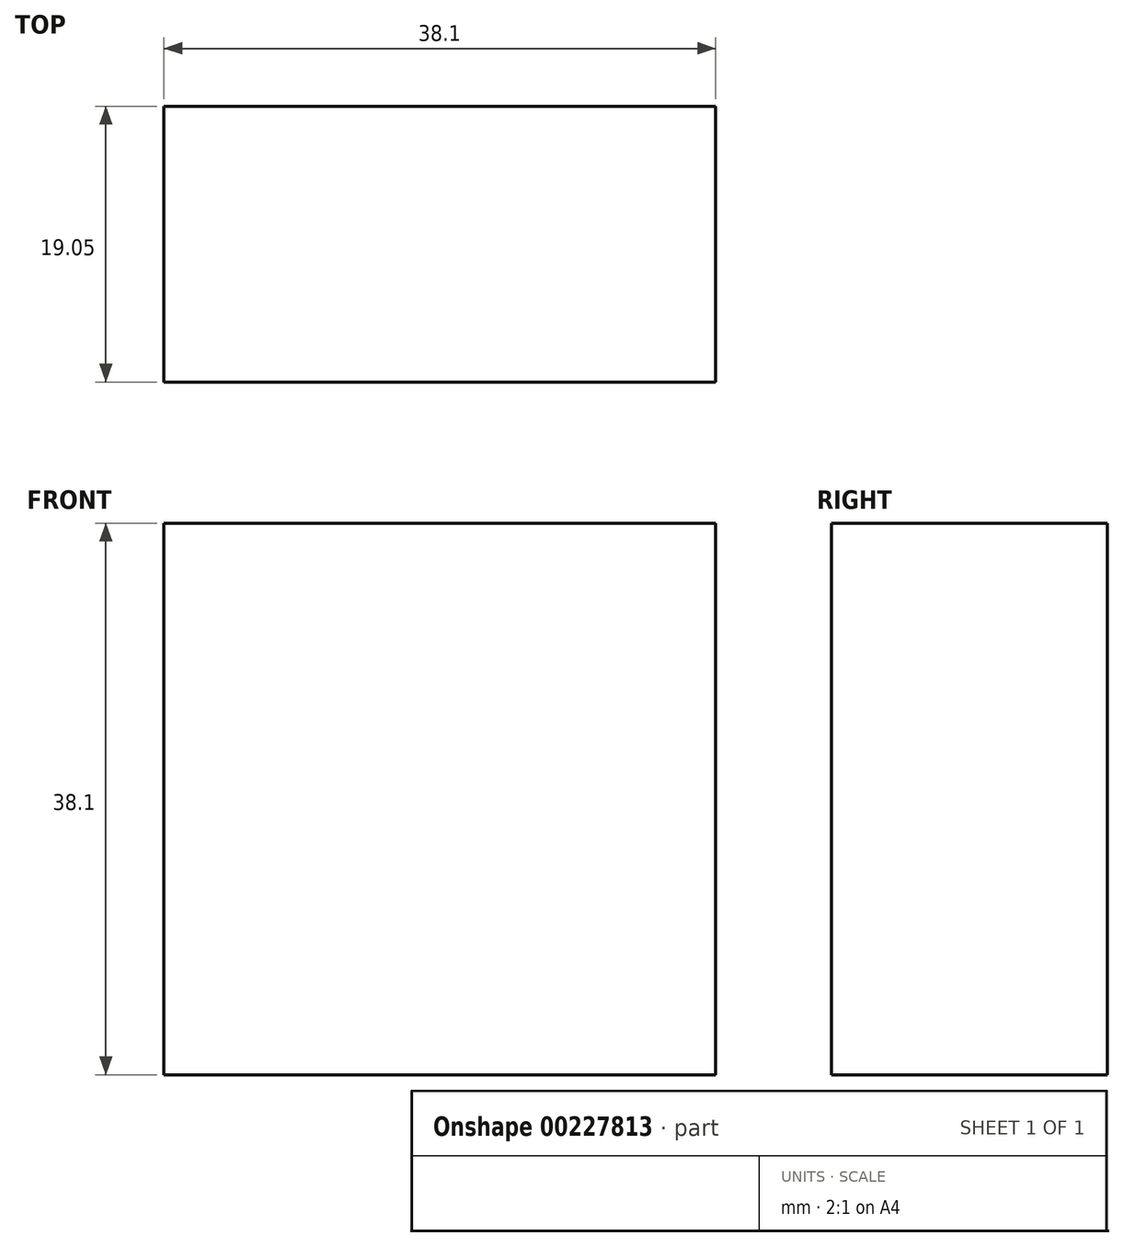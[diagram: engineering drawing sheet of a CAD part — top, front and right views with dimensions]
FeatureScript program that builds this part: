
annotation { "Feature Type Name" : "Feature", "Feature Type Description" : "" }
export const myFeature = defineFeature(function(context is Context, id is Id, definition is map)
    precondition{}
    {
        {
            var Q0;
            Q0=qCreatedBy(makeId("Front.planeOp"),FACE);
            var sketch = newSketch(context, id + "F0", { "sketchPlane" : qUnion([Q0])});
            skLineSegment(sketch, "E0.bottom", {"start": v(-30.4, 27.13) * mm, "end": v(7.7, 27.13) * mm});
            skLineSegment(sketch, "E0.top", {"start": v(-30.4, -10.97) * mm, "end": v(7.7, -10.97) * mm});
            skLineSegment(sketch, "E0.left", {"start": v(-30.4, 27.13) * mm, "end": v(-30.4, -10.97) * mm});
            skLineSegment(sketch, "E0.right", {"start": v(7.7, 27.13) * mm, "end": v(7.7, -10.97) * mm});
            skSolve(sketch);
        }
        {
            var Q0;
            Q0=makeQuery(id+"F0.imprint","IMPRINT",FACE,{"disambiguationData":[TD([[makeQuery(id+"F0.imprint","IMPRINT",EDGE,{"derivedFrom":sQuery(id+"F0.wireOp",EDGE,"E0.bottom")}),-1.0]])]});
            extrude(context, id + "F1", {"entities" : qUnion([Q0]), "depth" : 19.05 * mm});
        }
    });
